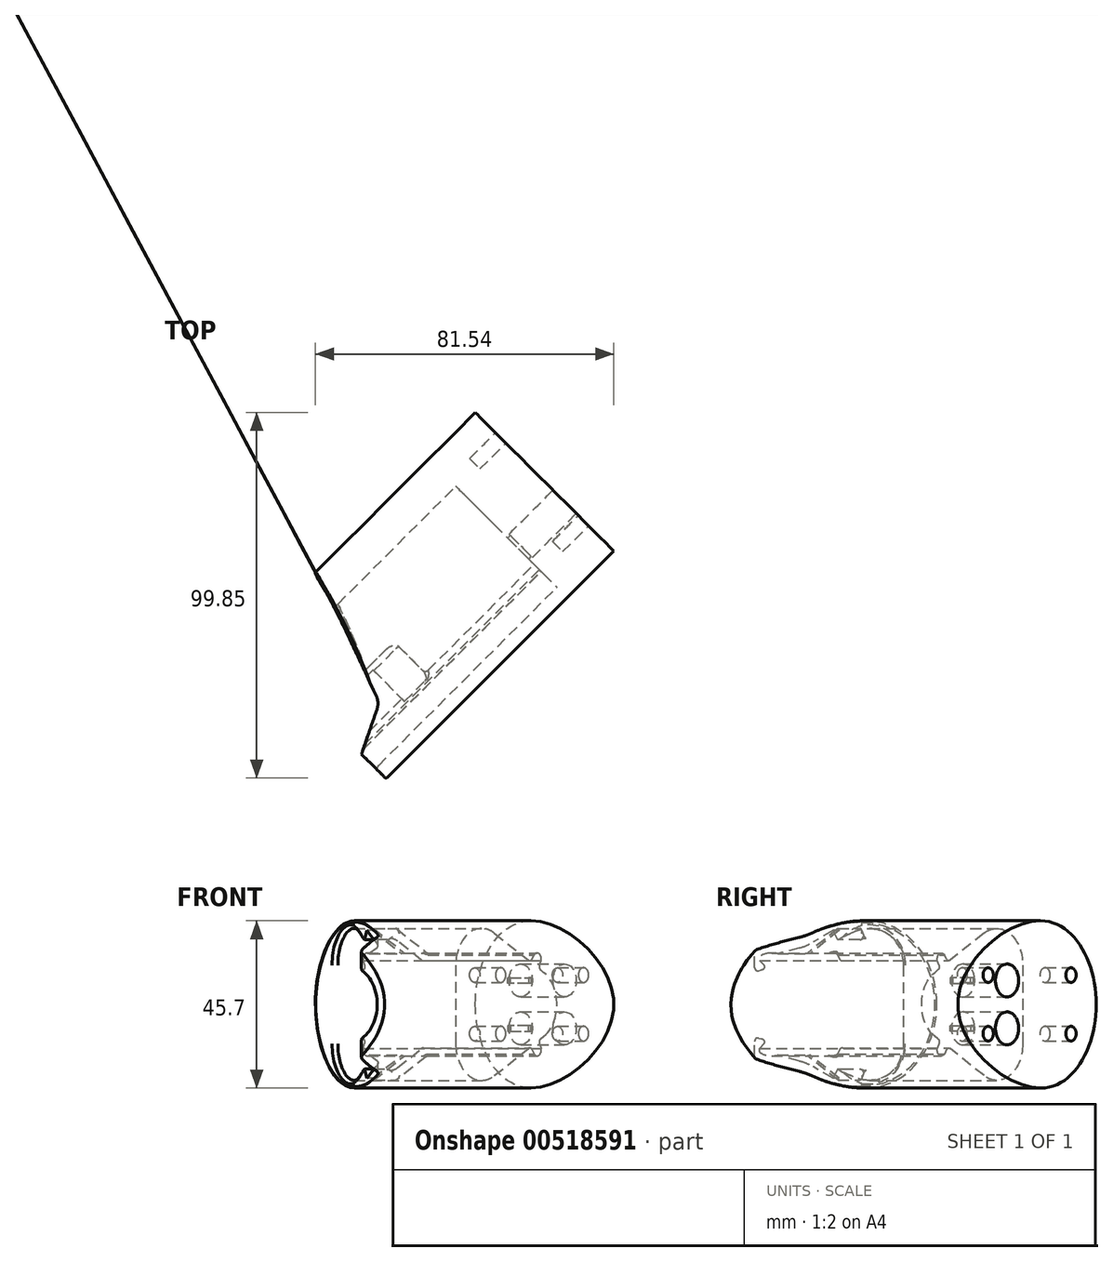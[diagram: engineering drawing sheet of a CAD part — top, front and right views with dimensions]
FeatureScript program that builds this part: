
annotation { "Feature Type Name" : "Feature", "Feature Type Description" : "" }
export const myFeature = defineFeature(function(context is Context, id is Id, definition is map)
    precondition{}
    {
        {
            var Q0;
            Q0=qCreatedBy(makeId("Top.planeOp"),FACE);
            var sketch = newSketch(context, id + "F0", { "sketchPlane" : qUnion([Q0])});
            skLineSegment(sketch, "E0", {"start": v(0, 0) * mm, "end": v(28.47, 0) * mm});
            skLineSegment(sketch, "E1", {"start": v(0, 0) * mm, "end": v(-67.18, -67.18) * mm});
            skLineSegment(sketch, "E2", {"start": v(-67.18, -67.18) * mm, "end": v(-77.25, -57.1) * mm});
            skSolve(sketch);
        }
        {
            var Q0;
            Q0=sQuery(id+"F0.wireOp",VERTEX,"E1.end");
            var Q1;
            Q1=sQuery(id+"F0.wireOp",EDGE,"E1");
            cPlane(context, id + "F1", {"entities" : qUnion([Q0, Q1]), "cplaneType" : CPlaneType.LINE_POINT, "offset" : 25 * mm, "width" : 150 * mm, "height" : 150 * mm});
        }
        {
            var Q0;
            Q0=qCreatedBy(id+"F1.planeOp",FACE);
            var sketch = newSketch(context, id + "F2", { "sketchPlane" : qUnion([Q0])});
            skFitSpline(sketch, "E3", {"points": [v(-61.79, 0) * mm, v(-42.33, 22.75) * mm, v(-8.29, 0) * mm, v(-42.33, -22.75) * mm, v(-61.79, 0) * mm]});
            skArc(sketch, "E4", {"start": v(-36.41, 19.46) * mm, "mid": v(-46.37, 19.39) * mm, "end": v(-51.33, 10.75) * mm});
            skArc(sketch, "E5.MirrorC", {"start": v(-36.41, -19.46) * mm, "mid": v(-46.37, -19.39) * mm, "end": v(-51.33, -10.75) * mm});
            skLineSegment(sketch, "E6", {"start": v(-51.33, 10.75) * mm, "end": v(-51.33, -10.75) * mm});
            skLineSegment(sketch, "E7", {"start": v(-22.48, 11.6) * mm, "end": v(-21.1, 13.55) * mm});
            skLineSegment(sketch, "E8", {"start": v(-22.48, 11.6) * mm, "end": v(-19.34, 9.82) * mm, "construction": true});
            skLineSegment(sketch, "E9", {"start": v(-19.34, 9.82) * mm, "end": v(-18.39, 12.02) * mm});
            skLineSegment(sketch, "E10.trimOffspring", {"start": v(-19.93, 12.45) * mm, "end": v(-20.91, 10.7) * mm, "construction": true});
            skArc(sketch, "E11", {"start": v(-18.39, 12.02) * mm, "mid": v(-19.14, 13.84) * mm, "end": v(-21.1, 13.55) * mm});
            skArc(sketch, "E12.trimOffspring", {"start": v(-17.37, -8.7) * mm, "mid": v(-12.29, 0) * mm, "end": v(-17.37, 8.7) * mm});
            skLineSegment(sketch, "E13", {"start": v(-36.41, 19.46) * mm, "end": v(-22.48, 11.6) * mm});
            skLineSegment(sketch, "E14", {"start": v(-19.34, 9.82) * mm, "end": v(-17.37, 8.7) * mm});
            skLineSegment(sketch, "E15", {"start": v(-22.29, 0) * mm, "end": v(-32.29, 0) * mm, "construction": true});
            skLineSegment(sketch, "E16.MirrorCS", {"start": v(-19.34, -9.82) * mm, "end": v(-18.39, -12.02) * mm});
            skArc(sketch, "E17.MirrorCS", {"start": v(-18.39, -12.02) * mm, "mid": v(-19.14, -13.84) * mm, "end": v(-21.1, -13.55) * mm});
            skLineSegment(sketch, "E18.MirrorCS", {"start": v(-22.48, -11.6) * mm, "end": v(-21.1, -13.55) * mm});
            skLineSegment(sketch, "E19.MirrorCS", {"start": v(-19.93, -12.45) * mm, "end": v(-20.91, -10.7) * mm, "construction": true});
            skLineSegment(sketch, "E20.MirrorCS", {"start": v(-22.48, -11.6) * mm, "end": v(-19.34, -9.82) * mm, "construction": true});
            skLineSegment(sketch, "E21.MirrorCS", {"start": v(-19.34, -9.82) * mm, "end": v(-17.37, -8.7) * mm});
            skLineSegment(sketch, "E22.MirrorCS", {"start": v(-36.41, -19.46) * mm, "end": v(-22.48, -11.6) * mm});
            skSolve(sketch);
        }
        {
            var Q0;
            {var subQ0=sQuery(id+"F2.wireOp",EDGE,"E3");var subQ2=sQuery(id+"F2.wireOp",EDGE,"pOtwqhd4-o26Y-xq34-vOwj-SUGbkzFwbKgE");var subQ4=makeQuery(id+"F2.imprint","INTERSECT",VERTEX,{"derivedFrom":[subQ2,subQ0]});Q0=makeQuery(id+"F2.imprint","IMPRINT",FACE,{"disambiguationData":[TD([[makeQuery(id+"F2.imprint","IMPRINT",EDGE,{"disambiguationData":[TD([[subQ4,-1.0]])],"derivedFrom":subQ2}),1.0]])]});}
            var Q1;
            {var subQ0=sQuery(id+"F2.wireOp",EDGE,"E3");var subQ2=sQuery(id+"F2.wireOp",EDGE,"gkpELcrs-MrsN-bJSW-tTVu-WertRLXtJEOw");var subQ4=makeQuery(id+"F2.imprint","INTERSECT",VERTEX,{"derivedFrom":[subQ2,subQ0]});Q1=makeQuery(id+"F2.imprint","IMPRINT",FACE,{"disambiguationData":[TD([[makeQuery(id+"F2.imprint","IMPRINT",EDGE,{"disambiguationData":[TD([[subQ4,1.0]])],"derivedFrom":subQ2}),1.0]])]});}
            var Q2;
            {var subQ0=sQuery(id+"F2.wireOp",EDGE,"E3");var subQ3=sQuery(id+"F2.wireOp",EDGE,"7pIhmMLG-Fg15-jHnL-DqUu-SUsHQT2I18XG");var subQ5=makeQuery(id+"F2.imprint","INTERSECT",VERTEX,{"derivedFrom":[subQ3,subQ0]});Q2=makeQuery(id+"F2.imprint","IMPRINT",FACE,{"disambiguationData":[TD([[makeQuery(id+"F2.imprint","IMPRINT",EDGE,{"disambiguationData":[TD([[subQ5,-1.0]])],"derivedFrom":subQ3}),-1.0]])]});}
            var Q3;
            {var subQ0=sQuery(id+"F2.wireOp",EDGE,"E3");var subQ3=sQuery(id+"F2.wireOp",EDGE,"7pIhmMLG-Fg15-jHnL-DqUu-SUsHQT2I18XG");var subQ5=makeQuery(id+"F2.imprint","INTERSECT",VERTEX,{"derivedFrom":[subQ3,subQ0]});Q3=makeQuery(id+"F2.imprint","IMPRINT",FACE,{"disambiguationData":[TD([[makeQuery(id+"F2.imprint","IMPRINT",EDGE,{"disambiguationData":[TD([[subQ5,-1.0]])],"derivedFrom":subQ3}),1.0]])]});}
            var Q4;
            Q4=makeQuery(id+"F2.imprint","IMPRINT",FACE,{"disambiguationData":[TD([[makeQuery(id+"F2.imprint","IMPRINT",EDGE,{"derivedFrom":sQuery(id+"F2.wireOp",EDGE,"E3")}),-1.0]])]});
            extrude(context, id + "F3", {"entities" : qUnion([Q0, Q1, Q2, Q3, Q4]), "depth" : 33 * mm});
        }
        {
            var Q0;
            Q0=qCreatedBy(makeId("Top.planeOp"),FACE);
            var sketch = newSketch(context, id + "F4", { "sketchPlane" : qUnion([Q0])});
            skPoint(sketch, "E23.orphan", {"position": v(-134.2, -46.82) * mm});
            skLineSegment(sketch, "E24", {"start": v(-99.06, -61.98) * mm, "end": v(-105.3, -48.64) * mm});
            skLineSegment(sketch, "E25", {"start": v(-103.09, -77.93) * mm, "end": v(-134.2, -46.82) * mm});
            skArc(sketch, "E26.filletArc", {"start": v(-98.86, -65.73) * mm, "mid": v(-98.6, -63.84) * mm, "end": v(-99.06, -61.98) * mm});
            skLineSegment(sketch, "E27", {"start": v(-134.2, -46.82) * mm, "end": v(-115.82, -28.43) * mm});
            skLineSegment(sketch, "E28", {"start": v(-103.09, -77.93) * mm, "end": v(-98.86, -65.73) * mm});
            skArc(sketch, "E29", {"start": v(-105.3, -48.64) * mm, "mid": v(-110.24, -38.37) * mm, "end": v(-115.82, -28.43) * mm});
            skSolve(sketch);
        }
        {
            var Q0;
            Q0=qSketchRegion(id+"F4",true);
            extrude(context, id + "F5", {"entities" : qUnion([Q0]), "operationType" : NewBodyOperationType.REMOVE, "oppositeDirection" : true, "depth" : 117.8 * mm, "symmetric" : true});
        }
        {
            var Q0;
            Q0=makeQuery(id+"F3.opExtrude","CAP_FACE",FACE,{"disambiguationData":[OSD([sQuery(id+"F2.wireOp",EDGE,"E3"),sQuery(id+"F2.wireOp",EDGE,"E4"),sQuery(id+"F2.wireOp",EDGE,"E5.MirrorC"),sQuery(id+"F2.wireOp",EDGE,"E6"),sQuery(id+"F2.wireOp",EDGE,"E7"),sQuery(id+"F2.wireOp",EDGE,"E9"),sQuery(id+"F2.wireOp",EDGE,"E11"),sQuery(id+"F2.wireOp",EDGE,"E12.trimOffspring"),sQuery(id+"F2.wireOp",EDGE,"E13"),sQuery(id+"F2.wireOp",EDGE,"E14"),sQuery(id+"F2.wireOp",EDGE,"E16.MirrorCS"),sQuery(id+"F2.wireOp",EDGE,"E17.MirrorCS"),sQuery(id+"F2.wireOp",EDGE,"E18.MirrorCS"),sQuery(id+"F2.wireOp",EDGE,"E21.MirrorCS"),sQuery(id+"F2.wireOp",EDGE,"E22.MirrorCS")])],"isStart":false});
            var sketch = newSketch(context, id + "F6", { "sketchPlane" : qUnion([Q0])});
            skLineSegment(sketch, "E30", {"start": v(-22.05, 10.04) * mm, "end": v(-20.08, 13.52) * mm});
            skLineSegment(sketch, "E31", {"start": v(-20.08, 13.52) * mm, "end": v(-31.84, 20.16) * mm});
            skLineSegment(sketch, "E32", {"start": v(-31.84, 20.16) * mm, "end": v(-33.8, 16.68) * mm});
            skLineSegment(sketch, "E33", {"start": v(-33.8, 16.68) * mm, "end": v(-22.05, 10.04) * mm});
            skPoint(sketch, "E34.0", {"position": v(-12.29, 0) * mm});
            skLineSegment(sketch, "E35", {"start": v(-12.29, 0) * mm, "end": v(-47.49, 0) * mm, "construction": true});
            skLineSegment(sketch, "E36.MirrorCS", {"start": v(-33.8, -16.68) * mm, "end": v(-22.05, -10.04) * mm});
            skLineSegment(sketch, "E37.MirrorCS", {"start": v(-22.05, -10.04) * mm, "end": v(-20.08, -13.52) * mm});
            skLineSegment(sketch, "E38.MirrorCS", {"start": v(-20.08, -13.52) * mm, "end": v(-31.84, -20.16) * mm});
            skLineSegment(sketch, "E39.MirrorCS", {"start": v(-31.84, -20.16) * mm, "end": v(-33.8, -16.68) * mm});
            skSolve(sketch);
        }
        {
            var Q0;
            Q0=qSketchRegion(id+"F6",true);
            extrude(context, id + "F7", {"entities" : qUnion([Q0]), "operationType" : NewBodyOperationType.REMOVE, "oppositeDirection" : true, "depth" : 28 * mm});
        }
        {
            var Q0;
            Q0=makeQuery(id+"F7.boolean.opBoolean","COPY",FACE,{"derivedFrom":makeQuery(id+"F7.opExtrude","CAP_FACE",FACE,{"disambiguationData":[OSD([sQuery(id+"F6.wireOp",EDGE,"E30"),sQuery(id+"F6.wireOp",EDGE,"E31"),sQuery(id+"F6.wireOp",EDGE,"E32"),sQuery(id+"F6.wireOp",EDGE,"E33")])],"isStart":false})});
            var sketch = newSketch(context, id + "F8", { "sketchPlane" : qUnion([Q0])});
            skLineSegment(sketch, "E40.0", {"start": v(-33.24, 17.67) * mm, "end": v(-33.24, 17.67) * mm});
            skLineSegment(sketch, "E41", {"start": v(-33.24, 17.67) * mm, "end": v(-31.52, 20.72) * mm});
            skLineSegment(sketch, "E42", {"start": v(-31.52, 20.72) * mm, "end": v(-31.52, 20.72) * mm});
            skLineSegment(sketch, "E43", {"start": v(-31.52, 20.72) * mm, "end": v(-33.24, 17.67) * mm});
            skPoint(sketch, "E44.0", {"position": v(-12.29, 0) * mm});
            skLineSegment(sketch, "E45", {"start": v(-12.29, 0) * mm, "end": v(-22.29, 0) * mm, "construction": true});
            skLineSegment(sketch, "E46.MirrorCS", {"start": v(-31.52, -20.72) * mm, "end": v(-33.24, -17.67) * mm});
            skLineSegment(sketch, "E47.MirrorCS", {"start": v(-33.24, -17.67) * mm, "end": v(-31.52, -20.72) * mm});
            skLineSegment(sketch, "E48.MirrorCS", {"start": v(-33.24, -17.67) * mm, "end": v(-33.24, -17.67) * mm});
            skLineSegment(sketch, "E49.MirrorCS", {"start": v(-31.52, -20.72) * mm, "end": v(-31.52, -20.72) * mm});
            skLineSegment(sketch, "E50", {"start": v(-31.52, 20.72) * mm, "end": v(-19.33, 13.83) * mm});
            skLineSegment(sketch, "E51", {"start": v(-19.33, 13.83) * mm, "end": v(-21.05, 10.79) * mm});
            skLineSegment(sketch, "E52", {"start": v(-21.05, 10.79) * mm, "end": v(-33.24, 17.67) * mm});
            skLineSegment(sketch, "E53.MirrorCS", {"start": v(-19.33, -13.83) * mm, "end": v(-21.05, -10.79) * mm});
            skLineSegment(sketch, "E54.MirrorCS", {"start": v(-31.52, -20.72) * mm, "end": v(-19.33, -13.83) * mm});
            skLineSegment(sketch, "E55.MirrorCS", {"start": v(-21.05, -10.79) * mm, "end": v(-33.24, -17.67) * mm});
            skSolve(sketch);
        }
        {
            var Q0;
            Q0=qSketchRegion(id+"F8",true);
            extrude(context, id + "F9", {"entities" : qUnion([Q0]), "operationType" : NewBodyOperationType.REMOVE, "depth" : 9.5 * mm});
        }
        {
            var Q0;
            Q0=makeQuery(id+"F3.opExtrude","CAP_FACE",FACE,{"disambiguationData":[OSD([sQuery(id+"F2.wireOp",EDGE,"E3"),sQuery(id+"F2.wireOp",EDGE,"E4"),sQuery(id+"F2.wireOp",EDGE,"E5.MirrorC"),sQuery(id+"F2.wireOp",EDGE,"E6"),sQuery(id+"F2.wireOp",EDGE,"E7"),sQuery(id+"F2.wireOp",EDGE,"E9"),sQuery(id+"F2.wireOp",EDGE,"E11"),sQuery(id+"F2.wireOp",EDGE,"E12.trimOffspring"),sQuery(id+"F2.wireOp",EDGE,"E13"),sQuery(id+"F2.wireOp",EDGE,"E14"),sQuery(id+"F2.wireOp",EDGE,"E16.MirrorCS"),sQuery(id+"F2.wireOp",EDGE,"E17.MirrorCS"),sQuery(id+"F2.wireOp",EDGE,"E18.MirrorCS"),sQuery(id+"F2.wireOp",EDGE,"E21.MirrorCS"),sQuery(id+"F2.wireOp",EDGE,"E22.MirrorCS")])],"isStart":true});
            extrude(context, id + "F10", {"entities" : qUnion([Q0]), "operationType" : NewBodyOperationType.ADD, "depth" : 55 * mm});
        }
        {
            var Q0;
            Q0=makeQuery(id+"F3.opExtrude","CAP_FACE",FACE,{"disambiguationData":[OSD([sQuery(id+"F2.wireOp",EDGE,"E3"),sQuery(id+"F2.wireOp",EDGE,"E4"),sQuery(id+"F2.wireOp",EDGE,"E5.MirrorC"),sQuery(id+"F2.wireOp",EDGE,"E6"),sQuery(id+"F2.wireOp",EDGE,"E7"),sQuery(id+"F2.wireOp",EDGE,"E9"),sQuery(id+"F2.wireOp",EDGE,"E11"),sQuery(id+"F2.wireOp",EDGE,"E12.trimOffspring"),sQuery(id+"F2.wireOp",EDGE,"E13"),sQuery(id+"F2.wireOp",EDGE,"E14"),sQuery(id+"F2.wireOp",EDGE,"E16.MirrorCS"),sQuery(id+"F2.wireOp",EDGE,"E17.MirrorCS"),sQuery(id+"F2.wireOp",EDGE,"E18.MirrorCS"),sQuery(id+"F2.wireOp",EDGE,"E21.MirrorCS"),sQuery(id+"F2.wireOp",EDGE,"E22.MirrorCS")])],"isStart":false});
            cPlane(context, id + "F11", {"entities" : qUnion([Q0]), "cplaneType" : CPlaneType.OFFSET, "offset" : 70 * mm, "oppositeDirection" : true, "width" : 150 * mm, "height" : 150 * mm});
        }
        {
            var Q0;
            Q0=qCreatedBy(id+"F11.planeOp",FACE);
            var sketch = newSketch(context, id + "F12", { "sketchPlane" : qUnion([Q0])});
            skLineSegment(sketch, "E56", {"start": v(-23.28, 5.8) * mm, "end": v(-31.28, 5.8) * mm});
            skLineSegment(sketch, "E57", {"start": v(-31.28, 5.8) * mm, "end": v(-31.28, 7.3) * mm});
            skLineSegment(sketch, "E58", {"start": v(-31.28, 7.3) * mm, "end": v(-23.28, 7.3) * mm});
            skLineSegment(sketch, "E59", {"start": v(-23.28, 7.3) * mm, "end": v(-23.28, 5.8) * mm});
            skLineSegment(sketch, "E60.MirrorCS", {"start": v(-23.28, -5.8) * mm, "end": v(-31.28, -5.8) * mm});
            skLineSegment(sketch, "E61.MirrorCS", {"start": v(-31.28, -7.3) * mm, "end": v(-23.28, -7.3) * mm});
            skLineSegment(sketch, "E62.MirrorCS", {"start": v(-23.28, -7.3) * mm, "end": v(-23.28, -5.8) * mm});
            skLineSegment(sketch, "E63.MirrorCS", {"start": v(-31.28, -5.8) * mm, "end": v(-31.28, -7.3) * mm});
            skPoint(sketch, "E64.0", {"position": v(-22.48, 11.6) * mm});
            skLineSegment(sketch, "E65.0", {"start": v(-51.33, 10.75) * mm, "end": v(-51.33, -10.75) * mm});
            skArc(sketch, "E66.0", {"start": v(-36.41, 19.46) * mm, "mid": v(-46.37, 19.39) * mm, "end": v(-51.33, 10.75) * mm});
            skArc(sketch, "E67.0", {"start": v(-36.41, -19.46) * mm, "mid": v(-46.37, -19.39) * mm, "end": v(-51.33, -10.75) * mm});
            skLineSegment(sketch, "E68.0", {"start": v(-36.41, 19.46) * mm, "end": v(-22.48, 11.6) * mm});
            skLineSegment(sketch, "E69.0", {"start": v(-22.48, 11.6) * mm, "end": v(-21.1, 13.55) * mm});
            skArc(sketch, "E70.0", {"start": v(-18.39, 12.02) * mm, "mid": v(-19.14, 13.84) * mm, "end": v(-21.1, 13.55) * mm});
            skLineSegment(sketch, "E71.0", {"start": v(-19.34, 9.82) * mm, "end": v(-18.39, 12.02) * mm});
            skLineSegment(sketch, "E72.0", {"start": v(-19.34, 9.82) * mm, "end": v(-17.37, 8.7) * mm});
            skArc(sketch, "E73.0", {"start": v(-17.37, -8.7) * mm, "mid": v(-12.29, 0) * mm, "end": v(-17.37, 8.7) * mm});
            skLineSegment(sketch, "E74.0", {"start": v(-19.34, -9.82) * mm, "end": v(-17.37, -8.7) * mm});
            skLineSegment(sketch, "E75.0", {"start": v(-19.34, -9.82) * mm, "end": v(-18.39, -12.02) * mm});
            skArc(sketch, "E76.0", {"start": v(-18.39, -12.02) * mm, "mid": v(-19.14, -13.84) * mm, "end": v(-21.1, -13.55) * mm});
            skLineSegment(sketch, "E77.0", {"start": v(-22.48, -11.6) * mm, "end": v(-21.1, -13.55) * mm});
            skLineSegment(sketch, "E78.0", {"start": v(-36.41, -19.46) * mm, "end": v(-22.48, -11.6) * mm});
            skLineSegment(sketch, "E79", {"start": v(-23.28, 5.8) * mm, "end": v(-31.28, 7.3) * mm, "construction": true});
            skSolve(sketch);
        }
        {
            var Q0;
            Q0=makeQuery(id+"F12.imprint","IMPRINT",FACE,{"disambiguationData":[TD([[makeQuery(id+"F12.imprint","IMPRINT",EDGE,{"derivedFrom":sQuery(id+"F12.wireOp",EDGE,"E56")}),1.0]])]});
            extrude(context, id + "F13", {"entities" : qUnion([Q0]), "operationType" : NewBodyOperationType.ADD, "oppositeDirection" : true, "depth" : 18 * mm});
        }
        {
            var Q0;
            Q0=makeQuery(id+"F3.opExtrude","CAP_EDGE",EDGE,{"disambiguationData":[OSD([sQuery(id+"F2.wireOp",EDGE,"E3")])],"isStart":false});
            var Q1;
            Q1=makeQuery(id+"F5.boolean.opBoolean","INTERSECT",EDGE,{"derivedFrom":[makeQuery(id+"F3.opExtrude","SWEPT_FACE",FACE,{"disambiguationData":[OSD([sQuery(id+"F2.wireOp",EDGE,"E3")])]}),makeQuery(id+"F5.opExtrude","SWEPT_FACE",FACE,{"disambiguationData":[OSD([sQuery(id+"F4.wireOp",EDGE,"E29")])]})]});
            fillet(context, id + "F14", {"entities" : qUnion([Q0, Q1]), "radius" : .5 * mm, "tangentPropagation" : true, "allowEdgeOverflow" : false});
        }
        {
            var Q0;
            Q0=makeQuery(id+"F13.boolean.opBoolean","MERGE",FACE,{"derivedFrom":[makeQuery(id+"F10.opExtrude","CAP_FACE",FACE,{"disambiguationData":[OSD([sQuery(id+"F2.wireOp",EDGE,"E3"),sQuery(id+"F2.wireOp",EDGE,"E4"),sQuery(id+"F2.wireOp",EDGE,"E5.MirrorC"),sQuery(id+"F2.wireOp",EDGE,"E6"),sQuery(id+"F2.wireOp",EDGE,"E7"),sQuery(id+"F2.wireOp",EDGE,"E9"),sQuery(id+"F2.wireOp",EDGE,"E11"),sQuery(id+"F2.wireOp",EDGE,"E12.trimOffspring"),sQuery(id+"F2.wireOp",EDGE,"E13"),sQuery(id+"F2.wireOp",EDGE,"E14"),sQuery(id+"F2.wireOp",EDGE,"E16.MirrorCS"),sQuery(id+"F2.wireOp",EDGE,"E17.MirrorCS"),sQuery(id+"F2.wireOp",EDGE,"E18.MirrorCS"),sQuery(id+"F2.wireOp",EDGE,"E21.MirrorCS"),sQuery(id+"F2.wireOp",EDGE,"E22.MirrorCS")])],"isStart":false}),makeQuery(id+"F13.opExtrude","CAP_FACE",FACE,{"disambiguationData":[OSD([sQuery(id+"F12.wireOp",EDGE,"E56"),sQuery(id+"F12.wireOp",EDGE,"E57"),sQuery(id+"F12.wireOp",EDGE,"E58"),sQuery(id+"F12.wireOp",EDGE,"E59"),sQuery(id+"F12.wireOp",EDGE,"E60.MirrorCS"),sQuery(id+"F12.wireOp",EDGE,"E61.MirrorCS"),sQuery(id+"F12.wireOp",EDGE,"E62.MirrorCS"),sQuery(id+"F12.wireOp",EDGE,"E63.MirrorCS"),sQuery(id+"F12.wireOp",EDGE,"E65.0"),sQuery(id+"F12.wireOp",EDGE,"E66.0"),sQuery(id+"F12.wireOp",EDGE,"E67.0"),sQuery(id+"F12.wireOp",EDGE,"E68.0"),sQuery(id+"F12.wireOp",EDGE,"E69.0"),sQuery(id+"F12.wireOp",EDGE,"E70.0"),sQuery(id+"F12.wireOp",EDGE,"E71.0"),sQuery(id+"F12.wireOp",EDGE,"E72.0"),sQuery(id+"F12.wireOp",EDGE,"E73.0"),sQuery(id+"F12.wireOp",EDGE,"E74.0"),sQuery(id+"F12.wireOp",EDGE,"E75.0"),sQuery(id+"F12.wireOp",EDGE,"E76.0"),sQuery(id+"F12.wireOp",EDGE,"E77.0"),sQuery(id+"F12.wireOp",EDGE,"E78.0")])],"isStart":false})]});
            var sketch = newSketch(context, id + "F15", { "sketchPlane" : qUnion([Q0])});
            skCircle(sketch, "E80", {"center": v(27.28, 6.54) * mm, "radius": 4.5 * mm});
            skLineSegment(sketch, "E81", {"start": v(31.28, 6.54) * mm, "end": v(23.28, 6.54) * mm, "construction": true});
            skCircle(sketch, "E82.MirrorC", {"center": v(27.28, -6.54) * mm, "radius": 4.5 * mm});
            skSolve(sketch);
        }
        {
            var Q0;
            Q0=qSketchRegion(id+"F15",true);
            extrude(context, id + "F16", {"entities" : qUnion([Q0]), "operationType" : NewBodyOperationType.REMOVE, "oppositeDirection" : true, "depth" : 17 * mm});
        }
        {
            var Q0;
            Q0=makeQuery(id+"F13.boolean.opBoolean","MERGE",FACE,{"derivedFrom":[makeQuery(id+"F10.opExtrude","CAP_FACE",FACE,{"disambiguationData":[OSD([sQuery(id+"F2.wireOp",EDGE,"E3"),sQuery(id+"F2.wireOp",EDGE,"E4"),sQuery(id+"F2.wireOp",EDGE,"E5.MirrorC"),sQuery(id+"F2.wireOp",EDGE,"E6"),sQuery(id+"F2.wireOp",EDGE,"E7"),sQuery(id+"F2.wireOp",EDGE,"E9"),sQuery(id+"F2.wireOp",EDGE,"E11"),sQuery(id+"F2.wireOp",EDGE,"E12.trimOffspring"),sQuery(id+"F2.wireOp",EDGE,"E13"),sQuery(id+"F2.wireOp",EDGE,"E14"),sQuery(id+"F2.wireOp",EDGE,"E16.MirrorCS"),sQuery(id+"F2.wireOp",EDGE,"E17.MirrorCS"),sQuery(id+"F2.wireOp",EDGE,"E18.MirrorCS"),sQuery(id+"F2.wireOp",EDGE,"E21.MirrorCS"),sQuery(id+"F2.wireOp",EDGE,"E22.MirrorCS")])],"isStart":false}),makeQuery(id+"F13.opExtrude","CAP_FACE",FACE,{"disambiguationData":[OSD([sQuery(id+"F12.wireOp",EDGE,"e2b537dc-d14d-47c2-8e2b-ed1ffd8bcd8d.0"),sQuery(id+"F12.wireOp",EDGE,"d1dbe5dc-4a35-4a4c-90cd-8f095bfceee0.0"),sQuery(id+"F12.wireOp",EDGE,"2784ca40-49a9-4d44-b39b-93614e9cc23b.0"),sQuery(id+"F12.wireOp",EDGE,"726b51e1-9b35-4e13-b5b2-7dae009988f0.0"),sQuery(id+"F12.wireOp",EDGE,"LQouA8SQ-tJYX-Ma9R-Kh6p-SBnR8ZIf9a8l"),sQuery(id+"F12.wireOp",EDGE,"E56"),sQuery(id+"F12.wireOp",EDGE,"E57"),sQuery(id+"F12.wireOp",EDGE,"E58"),sQuery(id+"F12.wireOp",EDGE,"E59"),sQuery(id+"F12.wireOp",EDGE,"E60.MirrorCS"),sQuery(id+"F12.wireOp",EDGE,"E61.MirrorCS"),sQuery(id+"F12.wireOp",EDGE,"E62.MirrorCS"),sQuery(id+"F12.wireOp",EDGE,"E63.MirrorCS"),sQuery(id+"F12.wireOp",EDGE,"1b76f597-295f-4c65-8000-a1490ce00d9a.0"),sQuery(id+"F12.wireOp",EDGE,"1c3e2adf-c9cf-4652-8e97-f62a4b036f38.0"),sQuery(id+"F12.wireOp",EDGE,"a5bbcf83-ce27-4e39-8dc8-a01f3983911c.0"),sQuery(id+"F12.wireOp",EDGE,"d850b7b5-e6ec-44aa-9d4d-e98d3fa20a65.0"),sQuery(id+"F12.wireOp",EDGE,"a50f8cc8-e1a2-4c80-a034-1cca13cb77f8.0"),sQuery(id+"F12.wireOp",EDGE,"0229090b-c308-4555-9769-62a321b65587.0"),sQuery(id+"F12.wireOp",EDGE,"f2301fbe-598b-4ec9-872f-e1c648518512.trimOffspring"),sQuery(id+"F12.wireOp",EDGE,"1ZlgNGct-iysy-SigZ-4Hng-N5hkl2DcCHdL"),sQuery(id+"F12.wireOp",EDGE,"Z9CZ6leL-Zrjv-R3xe-ZcaD-xpraGNOeYr1x")])],"isStart":false})]});
            var sketch = newSketch(context, id + "F17", { "sketchPlane" : qUnion([Q0])});
            skCircle(sketch, "E83", {"center": v(20, 8) * mm, "radius": 2 * mm});
            skCircle(sketch, "E84.MirrorC", {"center": v(20, -8) * mm, "radius": 2 * mm});
            skLineSegment(sketch, "E85", {"start": v(36, 12) * mm, "end": v(36, 0) * mm, "construction": true});
            skCircle(sketch, "E86.MirrorC", {"center": v(52, 8) * mm, "radius": 2 * mm});
            skCircle(sketch, "E87.MirrorC", {"center": v(52, -8) * mm, "radius": 2 * mm});
            skSolve(sketch);
        }
        {
            var Q0;
            Q0=qSketchRegion(id+"F17",true);
            extrude(context, id + "F18", {"entities" : qUnion([Q0]), "operationType" : NewBodyOperationType.REMOVE, "oppositeDirection" : true, "depth" : 20 * mm, "symmetric" : true});
        }
        {
            var Q0;
            Q0=makeQuery(id+"F3.opExtrude","CAP_EDGE",EDGE,{"disambiguationData":[OSD([sQuery(id+"F2.wireOp",EDGE,"E17.MirrorCS")])],"isStart":false});
            var Q1;
            Q1=makeQuery(id+"F3.opExtrude","CAP_EDGE",EDGE,{"disambiguationData":[OSD([sQuery(id+"F2.wireOp",EDGE,"E16.MirrorCS")])],"isStart":false});
            var Q2;
            Q2=makeQuery(id+"F3.opExtrude","CAP_EDGE",EDGE,{"disambiguationData":[OSD([sQuery(id+"F2.wireOp",EDGE,"E11")])],"isStart":false});
            var Q3;
            Q3=makeQuery(id+"F3.opExtrude","CAP_EDGE",EDGE,{"disambiguationData":[OSD([sQuery(id+"F2.wireOp",EDGE,"E9")])],"isStart":false});
            var Q4;
            Q4=makeQuery(id+"F3.opExtrude","CAP_EDGE",EDGE,{"disambiguationData":[OSD([sQuery(id+"F2.wireOp",EDGE,"E18.MirrorCS")])],"isStart":false});
            var Q5;
            Q5=makeQuery(id+"F5.boolean.opBoolean","INTERSECT",EDGE,{"derivedFrom":[makeQuery(id+"F3.opExtrude","SWEPT_FACE",FACE,{"disambiguationData":[OSD([sQuery(id+"F2.wireOp",EDGE,"E22.MirrorCS")])]}),makeQuery(id+"F5.opExtrude","SWEPT_FACE",FACE,{"disambiguationData":[OSD([sQuery(id+"F4.wireOp",EDGE,"j9s35o5q-he6P-4osg-dwql-8sYuHOqG0mMk")])]})]});
            var Q6;
            Q6=makeQuery(id+"F5.boolean.opBoolean","INTERSECT",EDGE,{"derivedFrom":[makeQuery(id+"F3.opExtrude","SWEPT_FACE",FACE,{"disambiguationData":[OSD([sQuery(id+"F2.wireOp",EDGE,"E18.MirrorCS")])]}),makeQuery(id+"F5.opExtrude","SWEPT_FACE",FACE,{"disambiguationData":[OSD([sQuery(id+"F4.wireOp",EDGE,"j9s35o5q-he6P-4osg-dwql-8sYuHOqG0mMk")])]})]});
            var Q7;
            Q7=makeQuery(id+"F3.opExtrude","CAP_EDGE",EDGE,{"disambiguationData":[OSD([sQuery(id+"F2.wireOp",EDGE,"E7")])],"isStart":false});
            var Q8;
            Q8=makeQuery(id+"F5.boolean.opBoolean","INTERSECT",EDGE,{"derivedFrom":[makeQuery(id+"F3.opExtrude","SWEPT_FACE",FACE,{"disambiguationData":[OSD([sQuery(id+"F2.wireOp",EDGE,"E13")])]}),makeQuery(id+"F5.opExtrude","SWEPT_FACE",FACE,{"disambiguationData":[OSD([sQuery(id+"F4.wireOp",EDGE,"j9s35o5q-he6P-4osg-dwql-8sYuHOqG0mMk")])]})]});
            var Q9;
            Q9=makeQuery(id+"F5.boolean.opBoolean","INTERSECT",EDGE,{"derivedFrom":[makeQuery(id+"F3.opExtrude","SWEPT_FACE",FACE,{"disambiguationData":[OSD([sQuery(id+"F2.wireOp",EDGE,"E6")])]}),makeQuery(id+"F5.opExtrude","SWEPT_FACE",FACE,{"disambiguationData":[OSD([sQuery(id+"F4.wireOp",EDGE,"E29")])]})]});
            var Q10;
            Q10=makeQuery(id+"F3.opExtrude","CAP_EDGE",EDGE,{"disambiguationData":[OSD([sQuery(id+"F2.wireOp",EDGE,"E12.trimOffspring")])],"isStart":false});
            var Q11;
            {var subQ0=sQuery(id+"F2.wireOp",EDGE,"E13");var subQ1=sQuery(id+"F2.wireOp",EDGE,"E7");Q11=makeQuery(id+"F10.boolean.opBoolean","MERGE",EDGE,{"derivedFrom":[makeQuery(id+"F3.opExtrude","SWEPT_EDGE",EDGE,{"disambiguationData":[OSD([subQ1,subQ0])]}),makeQuery(id+"F10.opExtrude","SWEPT_EDGE",EDGE,{"disambiguationData":[OSD([subQ1,subQ0])]})]});}
            var Q12;
            {var subQ0=sQuery(id+"F2.wireOp",EDGE,"E22.MirrorCS");var subQ1=sQuery(id+"F2.wireOp",EDGE,"E18.MirrorCS");Q12=makeQuery(id+"F10.boolean.opBoolean","MERGE",EDGE,{"derivedFrom":[makeQuery(id+"F3.opExtrude","SWEPT_EDGE",EDGE,{"disambiguationData":[OSD([subQ1,subQ0])]}),makeQuery(id+"F10.opExtrude","SWEPT_EDGE",EDGE,{"disambiguationData":[OSD([subQ1,subQ0])]})]});}
            var Q13;
            {var subQ0=sQuery(id+"F2.wireOp",EDGE,"E21.MirrorCS");var subQ1=sQuery(id+"F2.wireOp",EDGE,"E16.MirrorCS");Q13=makeQuery(id+"F10.boolean.opBoolean","MERGE",EDGE,{"derivedFrom":[makeQuery(id+"F3.opExtrude","SWEPT_EDGE",EDGE,{"disambiguationData":[OSD([subQ1,subQ0])]}),makeQuery(id+"F10.opExtrude","SWEPT_EDGE",EDGE,{"disambiguationData":[OSD([subQ1,subQ0])]})]});}
            var Q14;
            {var subQ0=sQuery(id+"F2.wireOp",EDGE,"E14");var subQ1=sQuery(id+"F2.wireOp",EDGE,"E9");Q14=makeQuery(id+"F10.boolean.opBoolean","MERGE",EDGE,{"derivedFrom":[makeQuery(id+"F3.opExtrude","SWEPT_EDGE",EDGE,{"disambiguationData":[OSD([subQ1,subQ0])]}),makeQuery(id+"F10.opExtrude","SWEPT_EDGE",EDGE,{"disambiguationData":[OSD([subQ1,subQ0])]})]});}
            var Q15;
            Q15=makeQuery(id+"F7.boolean.opBoolean","INTERSECT",EDGE,{"derivedFrom":[makeQuery(id+"F3.opExtrude","SWEPT_FACE",FACE,{"disambiguationData":[OSD([sQuery(id+"F2.wireOp",EDGE,"E13")])]}),makeQuery(id+"F7.opExtrude","CAP_FACE",FACE,{"disambiguationData":[OSD([sQuery(id+"F6.wireOp",EDGE,"E30"),sQuery(id+"F6.wireOp",EDGE,"E31"),sQuery(id+"F6.wireOp",EDGE,"E32"),sQuery(id+"F6.wireOp",EDGE,"E33")])],"isStart":false})]});
            var Q16;
            Q16=makeQuery(id+"F9.boolean.opBoolean","MERGE",FACE,{"derivedFrom":[makeQuery(id+"F7.boolean.opBoolean","COPY",FACE,{"derivedFrom":makeQuery(id+"F7.opExtrude","CAP_FACE",FACE,{"disambiguationData":[OSD([sQuery(id+"F6.wireOp",EDGE,"E36.MirrorCS"),sQuery(id+"F6.wireOp",EDGE,"E37.MirrorCS"),sQuery(id+"F6.wireOp",EDGE,"E38.MirrorCS"),sQuery(id+"F6.wireOp",EDGE,"E39.MirrorCS")])],"isStart":false})}),makeQuery(id+"F9.opExtrude","CAP_FACE",FACE,{"disambiguationData":[OSD([sQuery(id+"F8.wireOp",EDGE,"E53.MirrorCS"),sQuery(id+"F8.wireOp",EDGE,"E54.MirrorCS"),sQuery(id+"F8.wireOp",EDGE,"E46.MirrorCS"),sQuery(id+"F8.wireOp",EDGE,"E55.MirrorCS")])],"isStart":true})]});
            var Q17;
            Q17=makeQuery(id+"F9.boolean.opBoolean","MERGE",FACE,{"derivedFrom":[makeQuery(id+"F7.boolean.opBoolean","COPY",FACE,{"derivedFrom":makeQuery(id+"F7.opExtrude","CAP_FACE",FACE,{"disambiguationData":[OSD([sQuery(id+"F6.wireOp",EDGE,"E30"),sQuery(id+"F6.wireOp",EDGE,"E31"),sQuery(id+"F6.wireOp",EDGE,"E32"),sQuery(id+"F6.wireOp",EDGE,"E33")])],"isStart":false})}),makeQuery(id+"F9.opExtrude","CAP_FACE",FACE,{"disambiguationData":[OSD([sQuery(id+"F8.wireOp",EDGE,"E43"),sQuery(id+"F8.wireOp",EDGE,"E50"),sQuery(id+"F8.wireOp",EDGE,"E51"),sQuery(id+"F8.wireOp",EDGE,"E52")])],"isStart":true})]});
            fillet(context, id + "F19", {"entities" : qUnion([Q0, Q1, Q2, Q3, Q4, Q5, Q6, Q7, Q8, Q9, Q10, Q11, Q12, Q13, Q14, Q15, Q16, Q17]), "radius" : 1 * mm, "tangentPropagation" : true, "allowEdgeOverflow" : false});
        }
    });
